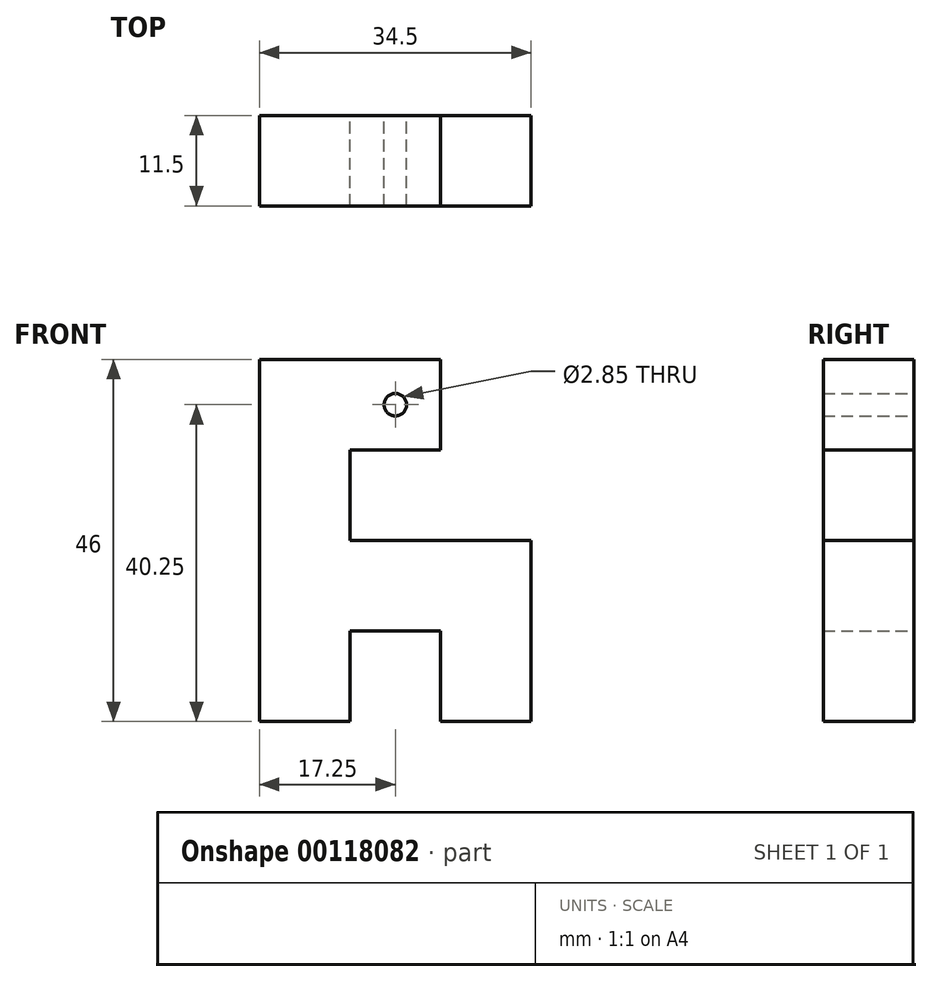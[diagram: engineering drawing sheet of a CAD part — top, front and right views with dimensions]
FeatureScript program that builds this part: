
annotation { "Feature Type Name" : "Feature", "Feature Type Description" : "" }
export const myFeature = defineFeature(function(context is Context, id is Id, definition is map)
    precondition{}
    {
        {
            var Q0;
            Q0=qCreatedBy(makeId("Front.planeOp"),FACE);
            var sketch = newSketch(context, id + "F0", { "sketchPlane" : qUnion([Q0])});
            skLineSegment(sketch, "E0", {"start": v(0, 0) * mm, "end": v(11.5, 0) * mm});
            skLineSegment(sketch, "E1", {"start": v(11.5, 0) * mm, "end": v(11.5, 11.5) * mm});
            skLineSegment(sketch, "E2", {"start": v(11.5, 11.5) * mm, "end": v(23, 11.5) * mm});
            skLineSegment(sketch, "E3", {"start": v(23, 11.5) * mm, "end": v(23, 0) * mm});
            skLineSegment(sketch, "E4", {"start": v(23, 0) * mm, "end": v(34.5, 0) * mm});
            skLineSegment(sketch, "E5", {"start": v(34.5, 0) * mm, "end": v(34.5, 23) * mm});
            skLineSegment(sketch, "E6", {"start": v(34.5, 23) * mm, "end": v(11.5, 23) * mm});
            skLineSegment(sketch, "E7", {"start": v(11.5, 23) * mm, "end": v(11.5, 34.5) * mm});
            skLineSegment(sketch, "E8", {"start": v(11.5, 34.5) * mm, "end": v(23, 34.5) * mm});
            skLineSegment(sketch, "E9", {"start": v(23, 34.5) * mm, "end": v(23, 46) * mm});
            skLineSegment(sketch, "E10", {"start": v(23, 46) * mm, "end": v(0, 46) * mm});
            skLineSegment(sketch, "E11", {"start": v(0, 46) * mm, "end": v(0, 0) * mm});
            skCircle(sketch, "E12", {"center": v(17.25, 40.25) * mm, "radius": 1.43 * mm});
            skPoint(sketch, "E12.centerSnap0", {"position": v(23, 40.25) * mm});
            skPoint(sketch, "E12.centerSnap1", {"position": v(17.25, 34.5) * mm});
            skSolve(sketch);
        }
        {
            var Q0;
            Q0=makeQuery(id+"F0.imprint","IMPRINT",FACE,{"disambiguationData":[TD([[makeQuery(id+"F0.imprint","IMPRINT",EDGE,{"derivedFrom":sQuery(id+"F0.wireOp",EDGE,"E0")}),1.0]])]});
            extrude(context, id + "F1", {"entities" : qUnion([Q0]), "depth" : 11.5 * mm});
        }
    });
